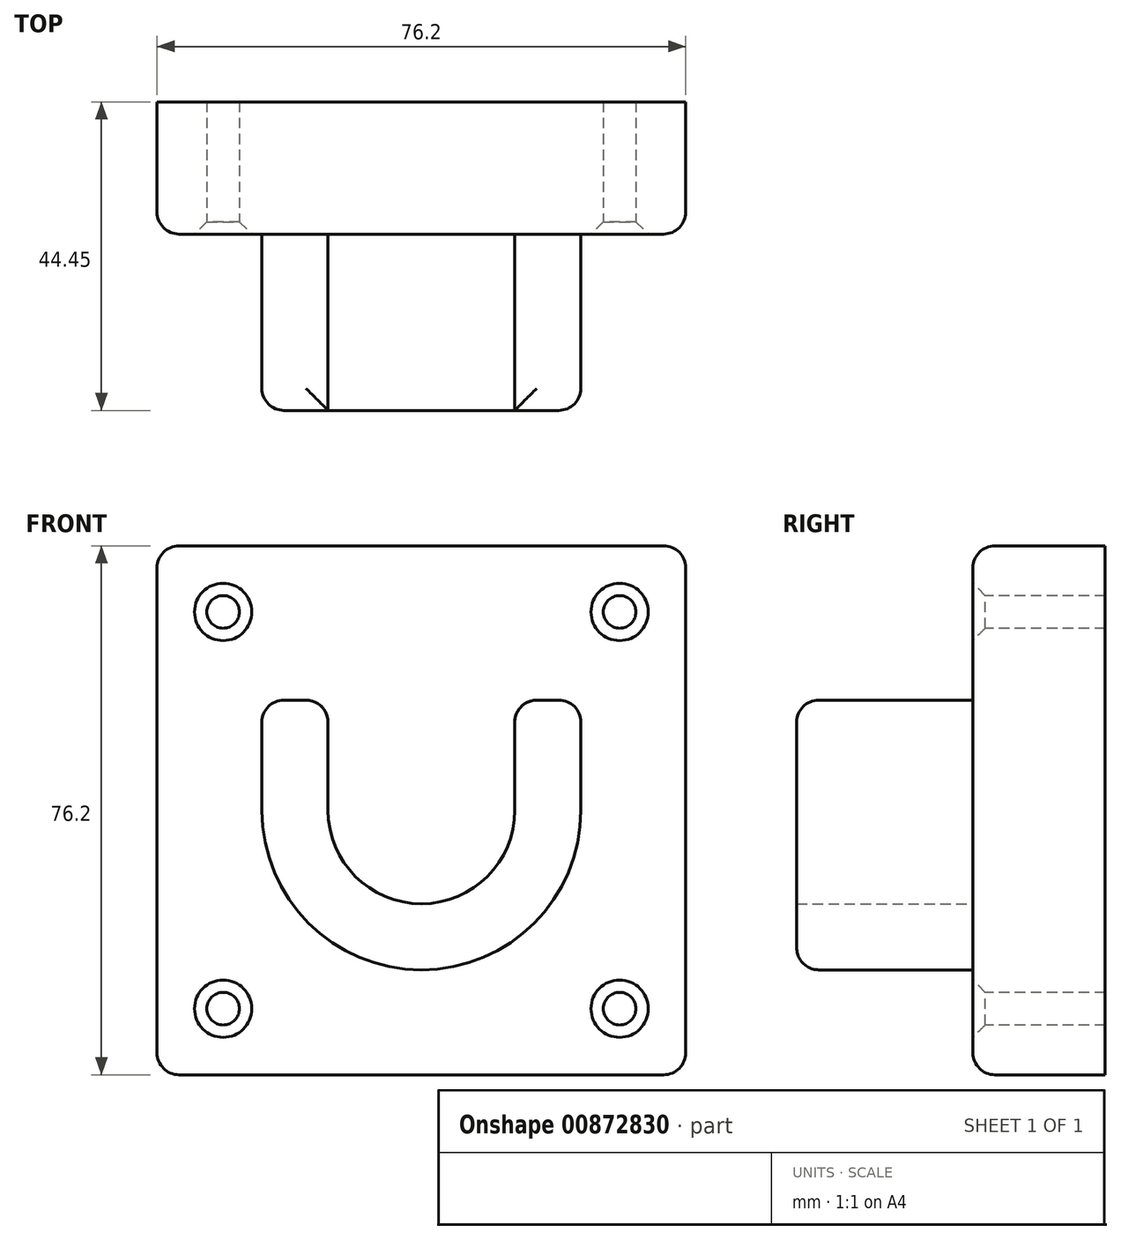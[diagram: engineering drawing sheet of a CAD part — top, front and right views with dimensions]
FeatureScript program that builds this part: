
annotation { "Feature Type Name" : "Feature", "Feature Type Description" : "" }
export const myFeature = defineFeature(function(context is Context, id is Id, definition is map)
    precondition{}
    {
        {
            var Q0;
            Q0=qCreatedBy(makeId("Front.planeOp"),FACE);
            var sketch = newSketch(context, id + "F0", { "sketchPlane" : qUnion([Q0])});
            skLineSegment(sketch, "E0.bottom", {"start": v(-38.1, 38.1) * mm, "end": v(38.1, 38.1) * mm});
            skLineSegment(sketch, "E0.top", {"start": v(-38.1, -38.1) * mm, "end": v(38.1, -38.1) * mm});
            skLineSegment(sketch, "E0.left", {"start": v(-38.1, 38.1) * mm, "end": v(-38.1, -38.1) * mm});
            skLineSegment(sketch, "E0.right", {"start": v(38.1, 38.1) * mm, "end": v(38.1, -38.1) * mm});
            skSolve(sketch);
        }
        {
            var Q0;
            Q0 = qSketchRegion(id + "F0", true);
            extrude(context, id + "F1", {"entities" : qUnion([Q0]), "depth" : 19.05 * mm, "offsetDistance" : 25.4 * mm});
        }
        {
            var Q0;
            Q0=makeQuery(id+"F1.opExtrude","CAP_FACE",FACE,{"disambiguationData":[OSD([sQuery(id+"F0.wireOp",EDGE,"E0.bottom"),sQuery(id+"F0.wireOp",EDGE,"E0.top"),sQuery(id+"F0.wireOp",EDGE,"E0.left"),sQuery(id+"F0.wireOp",EDGE,"E0.right")])],"isStart":false});
            var sketch = newSketch(context, id + "F2", { "sketchPlane" : qUnion([Q0])});
            skArc(sketch, "E1", {"start": v(-13.46, 0) * mm, "mid": v(0, -13.46) * mm, "end": v(13.46, 0) * mm});
            skLineSegment(sketch, "E2", {"start": v(44.54, 0) * mm, "end": v(-48.25, 0) * mm, "construction": true});
            skPoint(sketch, "E2.endSnap0", {"position": v(-38.1, 0) * mm});
            skArc(sketch, "E3", {"start": v(-22.99, 0) * mm, "mid": v(0, -22.99) * mm, "end": v(22.99, 0) * mm});
            skLineSegment(sketch, "E4", {"start": v(-49.17, 15.87) * mm, "end": v(49.73, 15.87) * mm, "construction": true});
            skLineSegment(sketch, "E5", {"start": v(-22.99, 0) * mm, "end": v(-22.99, 15.87) * mm});
            skLineSegment(sketch, "E6", {"start": v(-13.46, 0) * mm, "end": v(-13.46, 15.87) * mm});
            skLineSegment(sketch, "E7", {"start": v(-13.46, 15.87) * mm, "end": v(-22.99, 15.87) * mm});
            skLineSegment(sketch, "E8", {"start": v(13.46, 0) * mm, "end": v(13.46, 15.87) * mm});
            skLineSegment(sketch, "E9", {"start": v(22.99, 0) * mm, "end": v(22.99, 15.87) * mm});
            skLineSegment(sketch, "E10", {"start": v(22.99, 15.87) * mm, "end": v(13.46, 15.87) * mm});
            skSolve(sketch);
        }
        {
            var Q0;
            Q0=makeQuery(id+"F2.imprint","IMPRINT",FACE,{"disambiguationData":[TD([[makeQuery(id+"F2.imprint","IMPRINT",EDGE,{"derivedFrom":sQuery(id+"F2.wireOp",EDGE,"E1")}),-1.0]])]});
            extrude(context, id + "F3", {"entities" : qUnion([Q0]), "operationType" : NewBodyOperationType.ADD, "depth" : 25.4 * mm, "offsetDistance" : 25.4 * mm});
        }
        {
            var Q0;
            Q0=makeQuery(id+"F1.opExtrude","CAP_FACE",FACE,{"disambiguationData":[OSD([sQuery(id+"F0.wireOp",EDGE,"E0.bottom"),sQuery(id+"F0.wireOp",EDGE,"E0.top"),sQuery(id+"F0.wireOp",EDGE,"E0.left"),sQuery(id+"F0.wireOp",EDGE,"E0.right")])],"isStart":false});
            var sketch = newSketch(context, id + "F4", { "sketchPlane" : qUnion([Q0])});
            skPoint(sketch, "E11", {"position": v(-28.58, 28.58) * mm});
            skPoint(sketch, "E12", {"position": v(28.58, 28.58) * mm});
            skPoint(sketch, "E13", {"position": v(28.58, -28.57) * mm});
            skPoint(sketch, "E14", {"position": v(-28.58, -28.57) * mm});
            skSolve(sketch);
        }
        {
            var Q0;
            Q0=sQuery(id+"F4.wireOp",VERTEX,"E11");
            var Q1;
            Q1=sQuery(id+"F4.wireOp",VERTEX,"E12");
            var Q2;
            Q2=sQuery(id+"F4.wireOp",VERTEX,"E13");
            var Q3;
            Q3=sQuery(id+"F4.wireOp",VERTEX,"E14");
            var Q4;
            Q4=makeQuery(id+"F1.opExtrude","SWEPT_BODY",BODY,{"disambiguationData":[OSD([sQuery(id+"F0.wireOp",EDGE,"E0.bottom"),sQuery(id+"F0.wireOp",EDGE,"E0.top"),sQuery(id+"F0.wireOp",EDGE,"E0.left"),sQuery(id+"F0.wireOp",EDGE,"E0.right")])]});
            hole(context, id + "F5", {"style" : HoleStyle.C_SINK, "endStyle" : HoleEndStyle.THROUGH, "holeDiameter" : 4.7 * mm, "cSinkDiameter" : 8.25 * mm, "cSinkAngle" : 90 * degree, "majorDiameter" : 6.35 * mm, "isTappedThrough" : true, "tappedDepth" : 12.7 * mm, "tapClearance" : 3, "startFromSketch" : true, "locations" : qUnion([Q0, Q1, Q2, Q3]), "scope" : qUnion([Q4])});
        }
        {
            var Q0;
            Q0=makeQuery(id+"F1.opExtrude","CAP_EDGE",EDGE,{"disambiguationData":[OSD([sQuery(id+"F0.wireOp",EDGE,"E0.left")])],"isStart":false});
            var Q1;
            Q1=makeQuery(id+"F1.opExtrude","CAP_EDGE",EDGE,{"disambiguationData":[OSD([sQuery(id+"F0.wireOp",EDGE,"E0.bottom")])],"isStart":false});
            var Q2;
            Q2=makeQuery(id+"F1.opExtrude","CAP_EDGE",EDGE,{"disambiguationData":[OSD([sQuery(id+"F0.wireOp",EDGE,"E0.right")])],"isStart":false});
            var Q3;
            Q3=makeQuery(id+"F1.opExtrude","CAP_EDGE",EDGE,{"disambiguationData":[OSD([sQuery(id+"F0.wireOp",EDGE,"E0.top")])],"isStart":false});
            var Q4;
            Q4=makeQuery(id+"F3.opExtrude","CAP_EDGE",EDGE,{"disambiguationData":[OSD([sQuery(id+"F2.wireOp",EDGE,"E3")])],"isStart":false});
            var Q5;
            Q5=makeQuery(id+"F3.opExtrude","CAP_EDGE",EDGE,{"disambiguationData":[OSD([sQuery(id+"F2.wireOp",EDGE,"E3")])],"isStart":true});
            var Q6;
            Q6=makeQuery(id+"F1.opExtrude","SWEPT_EDGE",EDGE,{"disambiguationData":[OSD([sQuery(id+"F0.wireOp",EDGE,"E0.top"),sQuery(id+"F0.wireOp",EDGE,"E0.right")])]});
            var Q7;
            Q7=makeQuery(id+"F1.opExtrude","SWEPT_EDGE",EDGE,{"disambiguationData":[OSD([sQuery(id+"F0.wireOp",EDGE,"E0.bottom"),sQuery(id+"F0.wireOp",EDGE,"E0.right")])]});
            var Q8;
            Q8=makeQuery(id+"F1.opExtrude","SWEPT_EDGE",EDGE,{"disambiguationData":[OSD([sQuery(id+"F0.wireOp",EDGE,"E0.bottom"),sQuery(id+"F0.wireOp",EDGE,"E0.left")])]});
            var Q9;
            Q9=makeQuery(id+"F1.opExtrude","SWEPT_EDGE",EDGE,{"disambiguationData":[OSD([sQuery(id+"F0.wireOp",EDGE,"E0.top"),sQuery(id+"F0.wireOp",EDGE,"E0.left")])]});
            var Q10;
            Q10=makeQuery(id+"F3.opExtrude","SWEPT_EDGE",EDGE,{"disambiguationData":[OSD([sQuery(id+"F2.wireOp",EDGE,"E6"),sQuery(id+"F2.wireOp",EDGE,"E7")])]});
            var Q11;
            Q11=makeQuery(id+"F3.opExtrude","SWEPT_EDGE",EDGE,{"disambiguationData":[OSD([sQuery(id+"F2.wireOp",EDGE,"E8"),sQuery(id+"F2.wireOp",EDGE,"E10")])]});
            var Q12;
            Q12=makeQuery(id+"F3.opExtrude","SWEPT_EDGE",EDGE,{"disambiguationData":[OSD([sQuery(id+"F2.wireOp",EDGE,"E9"),sQuery(id+"F2.wireOp",EDGE,"E10")])]});
            var Q13;
            Q13=makeQuery(id+"F3.opExtrude","SWEPT_EDGE",EDGE,{"disambiguationData":[OSD([sQuery(id+"F2.wireOp",EDGE,"E5"),sQuery(id+"F2.wireOp",EDGE,"E7")])]});
            var Q14;
            Q14=makeQuery(id+"F3.opExtrude","CAP_EDGE",EDGE,{"disambiguationData":[OSD([sQuery(id+"F2.wireOp",EDGE,"E7")])],"isStart":false});
            var Q15;
            Q15=makeQuery(id+"F3.opExtrude","CAP_EDGE",EDGE,{"disambiguationData":[OSD([sQuery(id+"F2.wireOp",EDGE,"E10")])],"isStart":false});
            fillet(context, id + "F6", {"entities" : qUnion([Q0, Q1, Q2, Q3, Q4, Q5, Q6, Q7, Q8, Q9, Q10, Q11, Q12, Q13, Q14, Q15]), "radius" : 3.17 * mm, "tangentPropagation" : true, "allowEdgeOverflow" : false});
        }
    });
